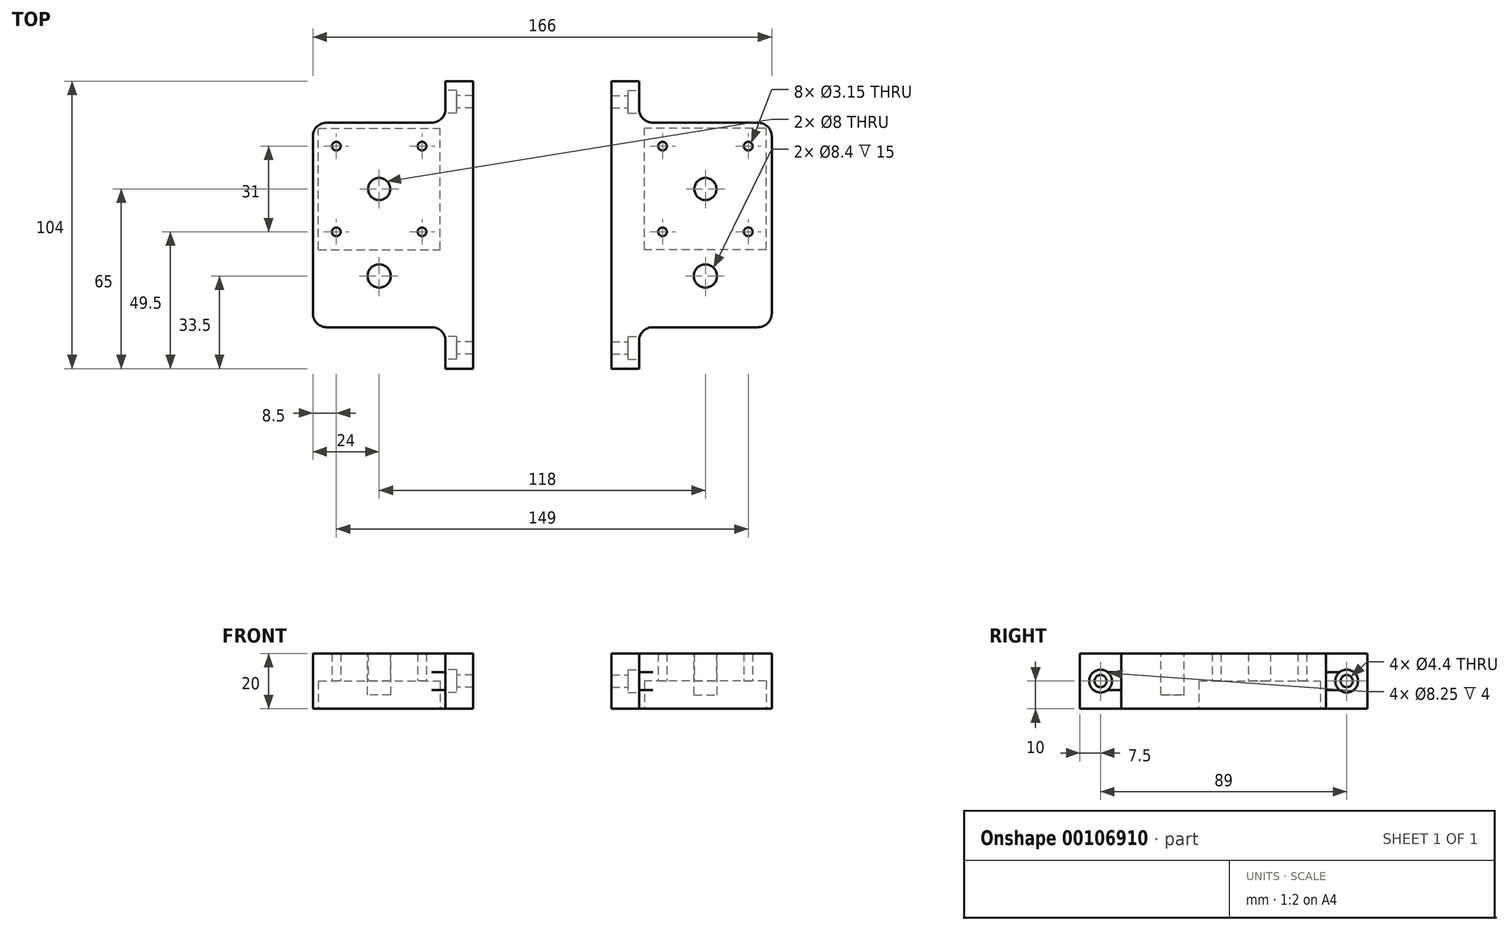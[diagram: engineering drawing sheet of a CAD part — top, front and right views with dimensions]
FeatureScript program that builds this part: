
annotation { "Feature Type Name" : "Feature", "Feature Type Description" : "" }
export const myFeature = defineFeature(function(context is Context, id is Id, definition is map)
    precondition{}
    {
        {
            var Q0;
            Q0=qCreatedBy(makeId("Top.planeOp"),FACE);
            var sketch = newSketch(context, id + "F0", { "sketchPlane" : qUnion([Q0])});
            skLineSegment(sketch, "E0.bottom", {"start": v(24, -37) * mm, "end": v(-24, -37) * mm});
            skLineSegment(sketch, "E0.top", {"start": v(24, 37) * mm, "end": v(-24, 37) * mm});
            skLineSegment(sketch, "E0.left", {"start": v(24, -37) * mm, "end": v(24, 37) * mm});
            skLineSegment(sketch, "E0.right", {"start": v(-24, -37) * mm, "end": v(-24, 37) * mm});
            skPoint(sketch, "E0.middle", {"position": v(0, 0) * mm});
            skCircle(sketch, "E1", {"center": v(-15.5, 28.5) * mm, "radius": 1.57 * mm});
            skCircle(sketch, "E2", {"center": v(15.5, 28.5) * mm, "radius": 1.57 * mm});
            skCircle(sketch, "E3", {"center": v(-15.5, -2.5) * mm, "radius": 1.57 * mm});
            skCircle(sketch, "E4", {"center": v(15.5, -2.5) * mm, "radius": 1.57 * mm});
            skLineSegment(sketch, "E5", {"start": v(-15.5, -2.5) * mm, "end": v(15.5, 28.5) * mm, "construction": true});
            skLineSegment(sketch, "E6", {"start": v(-15.5, 28.5) * mm, "end": v(15.5, -2.5) * mm, "construction": true});
            skPoint(sketch, "E7", {"position": v(0, 13) * mm});
            skCircle(sketch, "E8", {"center": v(0, 13) * mm, "radius": 4 * mm});
            skLineSegment(sketch, "E9.bottom", {"start": v(24, 52) * mm, "end": v(34, 52) * mm});
            skLineSegment(sketch, "E9.top", {"start": v(24, -52) * mm, "end": v(34, -52) * mm});
            skLineSegment(sketch, "E9.left", {"start": v(24, 52) * mm, "end": v(24, -52) * mm});
            skLineSegment(sketch, "E9.right", {"start": v(34, 52) * mm, "end": v(34, -52) * mm});
            skLineSegment(sketch, "E10", {"start": v(-24, 0) * mm, "end": v(24, -37) * mm, "construction": true});
            skLineSegment(sketch, "E11", {"start": v(-24, -37) * mm, "end": v(24, 0) * mm, "construction": true});
            skLineSegment(sketch, "E12.bottom", {"start": v(21.5, 34.5) * mm, "end": v(-21.5, 34.5) * mm, "construction": true});
            skLineSegment(sketch, "E12.top", {"start": v(21.5, -8.5) * mm, "end": v(-21.5, -8.5) * mm, "construction": true});
            skLineSegment(sketch, "E12.left", {"start": v(21.5, 34.5) * mm, "end": v(21.5, -8.5) * mm, "construction": true});
            skLineSegment(sketch, "E12.right", {"start": v(-21.5, 34.5) * mm, "end": v(-21.5, -8.5) * mm, "construction": true});
            skSolve(sketch);
        }
        {
            var Q0;
            Q0 = qSketchRegion(id + "F0", true);
            extrude(context, id + "F1", {"entities" : qUnion([Q0]), "depth" : 20 * mm});
        }
        {
            var Q0;
            Q0=makeQuery(id+"F1.opExtrude","CAP_FACE",FACE,{"disambiguationData":[OSD([sQuery(id+"F0.wireOp",EDGE,"E0.bottom"),sQuery(id+"F0.wireOp",EDGE,"E0.top"),sQuery(id+"F0.wireOp",EDGE,"E0.right"),sQuery(id+"F0.wireOp",EDGE,"E1"),sQuery(id+"F0.wireOp",EDGE,"E2"),sQuery(id+"F0.wireOp",EDGE,"E3"),sQuery(id+"F0.wireOp",EDGE,"E4"),sQuery(id+"F0.wireOp",EDGE,"E8"),sQuery(id+"F0.wireOp",EDGE,"E9.bottom"),sQuery(id+"F0.wireOp",EDGE,"E9.top"),sQuery(id+"F0.wireOp",EDGE,"E9.left"),sQuery(id+"F0.wireOp",EDGE,"E9.right")])],"isStart":false});
            var sketch = newSketch(context, id + "F2", { "sketchPlane" : qUnion([Q0])});
            skLineSegment(sketch, "E13", {"start": v(-24, 0) * mm, "end": v(24, -37) * mm, "construction": true});
            skLineSegment(sketch, "E14", {"start": v(24, -37) * mm, "end": v(24, 0) * mm, "construction": true});
            skLineSegment(sketch, "E15", {"start": v(24, 0) * mm, "end": v(-24, -37) * mm, "construction": true});
            skCircle(sketch, "E16", {"center": v(0, -18.5) * mm, "radius": 4.2 * mm});
            skSolve(sketch);
        }
        {
            var Q0;
            Q0 = qSketchRegion(id + "F2", true);
            extrude(context, id + "F3", {"entities" : qUnion([Q0]), "operationType" : NewBodyOperationType.REMOVE, "oppositeDirection" : true, "depth" : 15 * mm});
        }
        {
            var Q0;
            Q0=makeQuery(id+"F1.opExtrude","CAP_FACE",FACE,{"disambiguationData":[OSD([sQuery(id+"F0.wireOp",EDGE,"E0.bottom"),sQuery(id+"F0.wireOp",EDGE,"E0.top"),sQuery(id+"F0.wireOp",EDGE,"E0.right"),sQuery(id+"F0.wireOp",EDGE,"E1"),sQuery(id+"F0.wireOp",EDGE,"E2"),sQuery(id+"F0.wireOp",EDGE,"E3"),sQuery(id+"F0.wireOp",EDGE,"E4"),sQuery(id+"F0.wireOp",EDGE,"E8"),sQuery(id+"F0.wireOp",EDGE,"E9.bottom"),sQuery(id+"F0.wireOp",EDGE,"E9.top"),sQuery(id+"F0.wireOp",EDGE,"E9.left"),sQuery(id+"F0.wireOp",EDGE,"E9.right")])],"isStart":true});
            var sketch = newSketch(context, id + "F4", { "sketchPlane" : qUnion([Q0])});
            skLineSegment(sketch, "E17.bottom", {"start": v(-22, 9) * mm, "end": v(22, 9) * mm});
            skLineSegment(sketch, "E17.top", {"start": v(-22, -35) * mm, "end": v(22, -35) * mm});
            skLineSegment(sketch, "E17.left", {"start": v(-22, 9) * mm, "end": v(-22, -35) * mm});
            skLineSegment(sketch, "E17.right", {"start": v(22, 9) * mm, "end": v(22, -35) * mm});
            skLineSegment(sketch, "E18.bottom", {"start": v(15.5, 2.5) * mm, "end": v(-15.5, 2.5) * mm, "construction": true});
            skLineSegment(sketch, "E18.top", {"start": v(15.5, -28.5) * mm, "end": v(-15.5, -28.5) * mm, "construction": true});
            skLineSegment(sketch, "E18.left", {"start": v(15.5, 2.5) * mm, "end": v(15.5, -28.5) * mm, "construction": true});
            skLineSegment(sketch, "E18.right", {"start": v(-15.5, 2.5) * mm, "end": v(-15.5, -28.5) * mm, "construction": true});
            skPoint(sketch, "E18.middle", {"position": v(0, -13) * mm});
            skSolve(sketch);
        }
        {
            var Q0;
            Q0=makeQuery(id+"F4.imprint","IMPRINT",FACE,{"disambiguationData":[TD([[makeQuery(id+"F4.imprint","IMPRINT",EDGE,{"derivedFrom":sQuery(id+"F4.wireOp",EDGE,"E17.bottom")}),-1.0]])]});
            extrude(context, id + "F5", {"entities" : qUnion([Q0]), "operationType" : NewBodyOperationType.REMOVE, "oppositeDirection" : true, "depth" : 10 * mm});
        }
        {
            var Q0;
            {var subQ0=sQuery(id+"F0.wireOp",EDGE,"E9.left");Q0=makeQuery(id+"F1.opExtrude","SWEPT_FACE",FACE,{"disambiguationData":[OSD([subQ0]),TDD([makeQuery(id+"F0.imprint","IMPRINT",EDGE,{"disambiguationData":[TD([[makeQuery(id+"F0.imprint","INTERSECT",VERTEX,{"derivedFrom":[sQuery(id+"F0.wireOp",EDGE,"E0.bottom"),subQ0]}),-1.0]])],"derivedFrom":subQ0})])]});}
            var sketch = newSketch(context, id + "F6", { "sketchPlane" : qUnion([Q0])});
            skLineSegment(sketch, "E19", {"start": v(52, 20) * mm, "end": v(37, 0) * mm, "construction": true});
            skLineSegment(sketch, "E20", {"start": v(37, 20) * mm, "end": v(52, 0) * mm, "construction": true});
            skPoint(sketch, "E21", {"position": v(44.5, 10) * mm});
            skPoint(sketch, "E22.MirrorP", {"position": v(-44.5, 10) * mm});
            skSolve(sketch);
        }
        {
            var Q0;
            Q0=sQuery(id+"F6.wireOp",VERTEX,"E22.MirrorP");
            var Q1;
            Q1=sQuery(id+"F6.wireOp",VERTEX,"E21");
            var Q2;
            Q2=makeQuery(id+"F1.opExtrude","SWEPT_BODY",BODY,{"disambiguationData":[OSD([sQuery(id+"F0.wireOp",EDGE,"E0.bottom"),sQuery(id+"F0.wireOp",EDGE,"E0.top"),sQuery(id+"F0.wireOp",EDGE,"E0.right"),sQuery(id+"F0.wireOp",EDGE,"E1"),sQuery(id+"F0.wireOp",EDGE,"E2"),sQuery(id+"F0.wireOp",EDGE,"E3"),sQuery(id+"F0.wireOp",EDGE,"E4"),sQuery(id+"F0.wireOp",EDGE,"E8"),sQuery(id+"F0.wireOp",EDGE,"E9.bottom"),sQuery(id+"F0.wireOp",EDGE,"E9.top"),sQuery(id+"F0.wireOp",EDGE,"E9.left"),sQuery(id+"F0.wireOp",EDGE,"E9.right")])]});
            hole(context, id + "F7", {"style" : HoleStyle.C_BORE, "endStyle" : HoleEndStyle.THROUGH, "standardTappedOrClearance" : lookupTablePath({ "standard" : "ISO", "fit" : "Normal", "size" : "M4", "type" : "Clearance" }), "standardBlindInLast" : lookupTablePath({ "fit" : "Standard", "standard" : "ISO", "size" : "M4", "type" : "Clearance" }), "holeDiameter" : 4.4 * mm, "cBoreDiameter" : 8.25 * mm, "cBoreDepth" : 4 * mm, "locations" : qUnion([Q0, Q1]), "scope" : qUnion([Q2]), "isTappedThrough" : true});
        }
        {
            var Q0;
            Q0=makeQuery(id+"F1.opExtrude","SWEPT_EDGE",EDGE,{"disambiguationData":[OSD([sQuery(id+"F0.wireOp",EDGE,"E0.top"),sQuery(id+"F0.wireOp",EDGE,"E9.left")])]});
            var Q1;
            Q1=makeQuery(id+"F1.opExtrude","SWEPT_EDGE",EDGE,{"disambiguationData":[OSD([sQuery(id+"F0.wireOp",EDGE,"E0.top"),sQuery(id+"F0.wireOp",EDGE,"E0.right")])]});
            var Q2;
            Q2=makeQuery(id+"F1.opExtrude","SWEPT_EDGE",EDGE,{"disambiguationData":[OSD([sQuery(id+"F0.wireOp",EDGE,"E0.bottom"),sQuery(id+"F0.wireOp",EDGE,"E0.right")])]});
            var Q3;
            Q3=makeQuery(id+"F1.opExtrude","SWEPT_EDGE",EDGE,{"disambiguationData":[OSD([sQuery(id+"F0.wireOp",EDGE,"E0.bottom"),sQuery(id+"F0.wireOp",EDGE,"E9.left")])]});
            fillet(context, id + "F8", {"entities" : qUnion([Q0, Q1, Q2, Q3]), "radius" : 5 * mm, "tangentPropagation" : true, "allowEdgeOverflow" : false});
        }
        {
            var Q0;
            Q0=makeQuery(id+"F1.opExtrude","SWEPT_FACE",FACE,{"disambiguationData":[OSD([sQuery(id+"F0.wireOp",EDGE,"E9.right")])]});
            cPlane(context, id + "F9", {"entities" : qUnion([Q0]), "cplaneType" : CPlaneType.OFFSET, "offset" : 25 * mm, "width" : 150 * mm, "height" : 150 * mm});
        }
        {
            var Q0;
            Q0=makeQuery(id+"F1.opExtrude","SWEPT_BODY",BODY,{"disambiguationData":[OSD([sQuery(id+"F0.wireOp",EDGE,"E0.bottom"),sQuery(id+"F0.wireOp",EDGE,"E0.top"),sQuery(id+"F0.wireOp",EDGE,"E0.right"),sQuery(id+"F0.wireOp",EDGE,"E1"),sQuery(id+"F0.wireOp",EDGE,"E2"),sQuery(id+"F0.wireOp",EDGE,"E3"),sQuery(id+"F0.wireOp",EDGE,"E4"),sQuery(id+"F0.wireOp",EDGE,"E8"),sQuery(id+"F0.wireOp",EDGE,"E9.bottom"),sQuery(id+"F0.wireOp",EDGE,"E9.top"),sQuery(id+"F0.wireOp",EDGE,"E9.left"),sQuery(id+"F0.wireOp",EDGE,"E9.right")])]});
            var Q1;
            Q1=qCreatedBy(id+"F9.planeOp",FACE);
            mirror(context, id + "F10", {"entities" : qUnion([Q0]), "mirrorPlane" : qUnion([Q1])});
        }
    });
